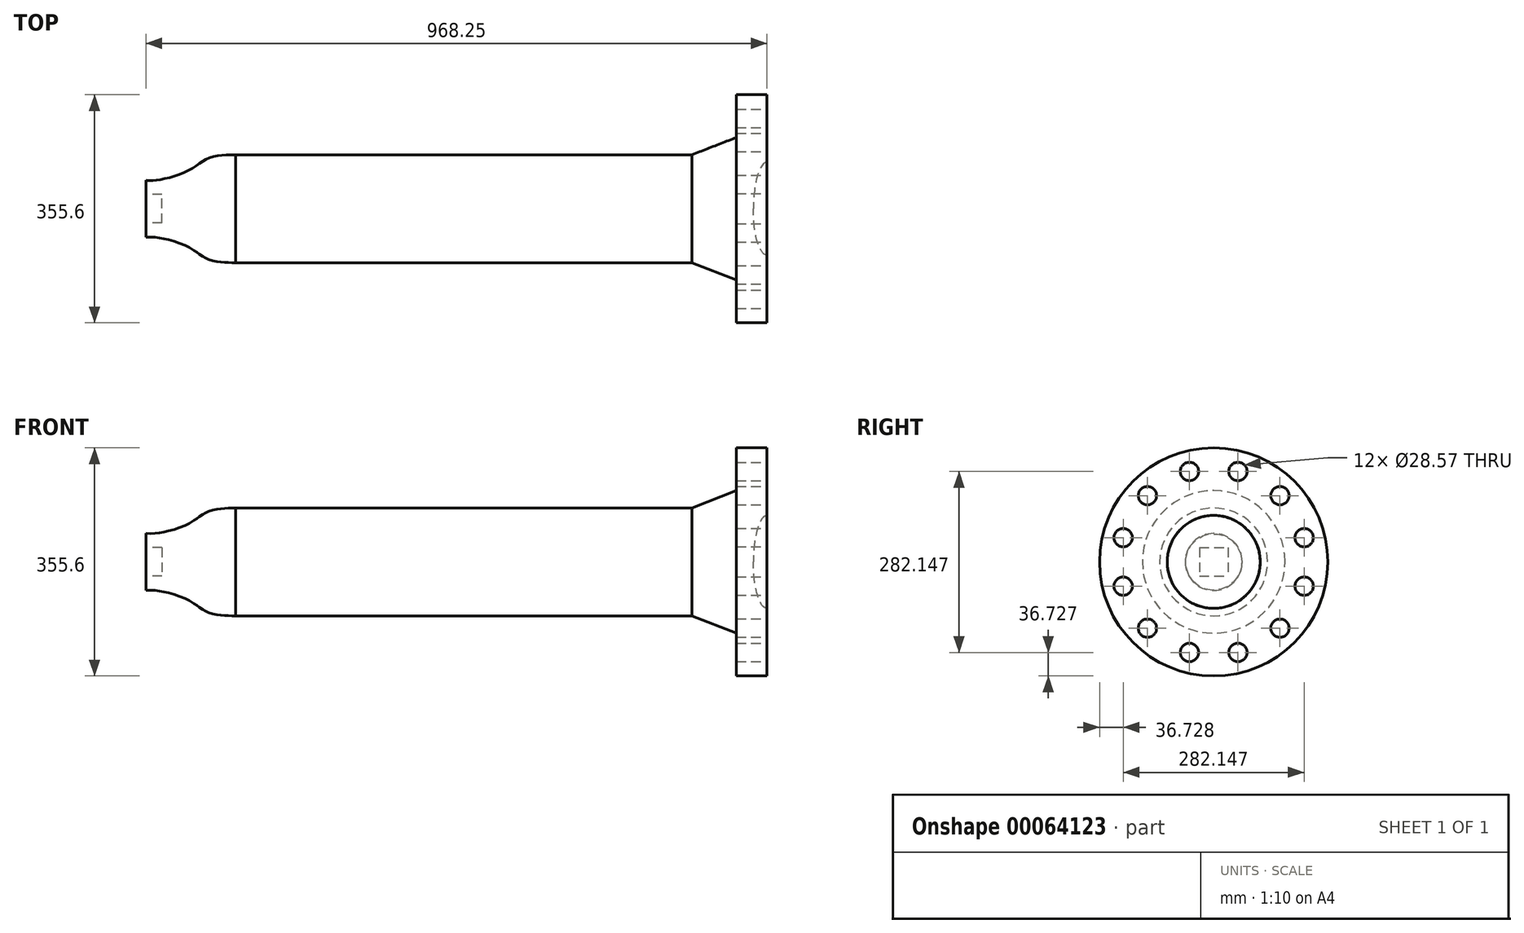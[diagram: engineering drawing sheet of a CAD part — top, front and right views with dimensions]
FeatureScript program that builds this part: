
annotation { "Feature Type Name" : "Feature", "Feature Type Description" : "" }
export const myFeature = defineFeature(function(context is Context, id is Id, definition is map)
    precondition{}
    {
        {
            var Q0;
            Q0=qCreatedBy(makeId("Top.planeOp"),FACE);
            var sketch = newSketch(context, id + "F0", { "sketchPlane" : qUnion([Q0])});
            skLineSegment(sketch, "E0.bottom", {"start": v(355.6, 55.78) * mm, "end": v(-355.6, 55.78) * mm});
            skLineSegment(sketch, "E0.left", {"start": v(355.6, 55.78) * mm, "end": v(355.6, -28.36) * mm});
            skLineSegment(sketch, "E0.right", {"start": v(-355.6, 55.78) * mm, "end": v(-355.6, -28.36) * mm});
            skPoint(sketch, "E0.middle", {"position": v(0, -28.36) * mm});
            skLineSegment(sketch, "E1", {"start": v(-355.6, -28.36) * mm, "end": v(-495.3, -28.36) * mm});
            skLineSegment(sketch, "E2", {"start": v(-495.3, -28.36) * mm, "end": v(-495.3, 16.1) * mm});
            skFitSpline(sketch, "E3", {"points": [v(-495.3, 16.1) * mm, v(-480.3, 16.1) * mm, v(-430.85, 30.2) * mm, v(-397.55, 50.39) * mm, v(-355.6, 55.78) * mm], "startDerivative": vector(75.86, -6.63) * mm, "endDerivative": vector(164.84, 3.12) * mm});
            skLineSegment(sketch, "E4", {"start": v(-355.6, -28.36) * mm, "end": v(355.6, -28.36) * mm});
            skLineSegment(sketch, "E5", {"start": v(0, 55.78) * mm, "end": v(0, -112.5) * mm, "construction": true});
            skLineSegment(sketch, "E6", {"start": v(355.6, -28.36) * mm, "end": v(472.95, -28.36) * mm});
            skLineSegment(sketch, "E7", {"start": v(472.95, -28.36) * mm, "end": v(472.95, 149.44) * mm});
            skLineSegment(sketch, "E8", {"start": v(472.95, 149.44) * mm, "end": v(425.2, 149.44) * mm});
            skLineSegment(sketch, "E9", {"start": v(425.2, 149.44) * mm, "end": v(425.2, 82.77) * mm});
            skLineSegment(sketch, "E10", {"start": v(425.2, 82.77) * mm, "end": v(355.6, 55.78) * mm});
            skEllipticalArc(sketch, "E11", {});
            const initialGuessF0  = {"E11": [0.472948, -0.028358574647295482, 0, 1, 0.07247824563442469, 0.021333515674718143, 0, 1.5707963267948966]};
            skSetInitialGuess(sketch, initialGuessF0);
            skSolve(sketch);
        }
        {
            var Q0;
            Q0=makeQuery(id+"F0.imprint","IMPRINT",FACE,{"disambiguationData":[TD([[makeQuery(id+"F0.imprint","IMPRINT",EDGE,{"derivedFrom":sQuery(id+"F0.wireOp",EDGE,"E0.right")}),-1.0]])]});
            var Q1;
            Q1=makeQuery(id+"F0.imprint","IMPRINT",FACE,{"disambiguationData":[TD([[makeQuery(id+"F0.imprint","IMPRINT",EDGE,{"derivedFrom":sQuery(id+"F0.wireOp",EDGE,"E0.bottom")}),1.0]])]});
            var Q2;
            Q2=makeQuery(id+"F0.imprint","IMPRINT",FACE,{"disambiguationData":[TD([[makeQuery(id+"F0.imprint","IMPRINT",EDGE,{"derivedFrom":sQuery(id+"F0.wireOp",EDGE,"E0.left")}),1.0]])]});
            var Q3;
            Q3=sQuery(id+"F0.wireOp",EDGE,"E1");
            revolve(context, id + "F1", {"entities" : qUnion([Q0, Q1, Q2]), "axis" : qUnion([Q3]), "revolveType" : RevolveType.FULL});
        }
        {
            var Q0;
            Q0=makeQuery(id+"F1.opRevolve","SWEPT_FACE",FACE,{"disambiguationData":[OSD([sQuery(id+"F0.wireOp",EDGE,"E2")])]});
            var sketch = newSketch(context, id + "F2", { "sketchPlane" : qUnion([Q0])});
            skLineSegment(sketch, "E12.bottom", {"start": v(50.58, 22.23) * mm, "end": v(6.13, 22.22) * mm});
            skLineSegment(sketch, "E12.top", {"start": v(50.58, -22.23) * mm, "end": v(6.13, -22.23) * mm});
            skLineSegment(sketch, "E12.left", {"start": v(50.58, 22.23) * mm, "end": v(50.58, -22.23) * mm});
            skLineSegment(sketch, "E12.right", {"start": v(6.13, 22.23) * mm, "end": v(6.13, -22.23) * mm});
            skPoint(sketch, "E12.middle", {"position": v(28.36, 0) * mm});
            skSolve(sketch);
        }
        {
            var Q0;
            Q0=makeQuery(id+"F2.imprint","IMPRINT",FACE,{"disambiguationData":[TD([[makeQuery(id+"F2.imprint","IMPRINT",EDGE,{"derivedFrom":sQuery(id+"F2.wireOp",EDGE,"E12.bottom")}),1.0]])]});
            extrude(context, id + "F3", {"entities" : qUnion([Q0]), "operationType" : NewBodyOperationType.REMOVE, "oppositeDirection" : true, "depth" : 25.4 * mm, "offsetDistance" : 25.4 * mm});
        }
        {
            var Q0;
            Q0=makeQuery(id+"F1.opRevolve","SWEPT_FACE",FACE,{"disambiguationData":[OSD([sQuery(id+"F0.wireOp",EDGE,"E7")])]});
            var sketch = newSketch(context, id + "F4", { "sketchPlane" : qUnion([Q0])});
            skCircle(sketch, "E13", {"center": v(-28.36, 0) * mm, "radius": 146.05 * mm, "construction": true});
            skLineSegment(sketch, "E14", {"start": v(-28.36, 0) * mm, "end": v(185.04, 0) * mm, "construction": true});
            skLineSegment(sketch, "E15", {"start": v(-28.36, 0) * mm, "end": v(183.38, 56.74) * mm, "construction": true});
            skCircle(sketch, "E16", {"center": v(112.71, 37.8) * mm, "radius": 14.29 * mm});
            skCircle(sketch, "E17.1.0", {"center": v(74.91, 103.27) * mm, "radius": 14.29 * mm});
            skCircle(sketch, "E17.2.0", {"center": v(9.44, 141.07) * mm, "radius": 14.29 * mm});
            skCircle(sketch, "E17.3.0", {"center": v(-66.16, 141.07) * mm, "radius": 14.29 * mm});
            skCircle(sketch, "E17.4.0", {"center": v(-131.63, 103.27) * mm, "radius": 14.29 * mm});
            skCircle(sketch, "E17.5.0", {"center": v(-169.43, 37.8) * mm, "radius": 14.29 * mm});
            skCircle(sketch, "E17.6.0", {"center": v(-169.43, -37.8) * mm, "radius": 14.29 * mm});
            skCircle(sketch, "E17.7.0", {"center": v(-131.63, -103.27) * mm, "radius": 14.29 * mm});
            skCircle(sketch, "E17.8.0", {"center": v(-66.16, -141.07) * mm, "radius": 14.29 * mm});
            skCircle(sketch, "E17.9.0", {"center": v(9.44, -141.07) * mm, "radius": 14.29 * mm});
            skCircle(sketch, "E17.10.0", {"center": v(74.91, -103.27) * mm, "radius": 14.29 * mm});
            skCircle(sketch, "E17.11.0", {"center": v(112.71, -37.8) * mm, "radius": 14.29 * mm});
            skSolve(sketch);
        }
        {
            var Q0;
            Q0=makeQuery(id+"F4.imprint","IMPRINT",FACE,{"disambiguationData":[TD([[makeQuery(id+"F4.imprint","IMPRINT",EDGE,{"derivedFrom":sQuery(id+"F4.wireOp",EDGE,"E17.4.0")}),1.0]])]});
            var Q1;
            Q1=makeQuery(id+"F4.imprint","IMPRINT",FACE,{"disambiguationData":[TD([[makeQuery(id+"F4.imprint","IMPRINT",EDGE,{"derivedFrom":sQuery(id+"F4.wireOp",EDGE,"E17.3.0")}),1.0]])]});
            var Q2;
            Q2=makeQuery(id+"F4.imprint","IMPRINT",FACE,{"disambiguationData":[TD([[makeQuery(id+"F4.imprint","IMPRINT",EDGE,{"derivedFrom":sQuery(id+"F4.wireOp",EDGE,"E17.2.0")}),1.0]])]});
            var Q3;
            Q3=makeQuery(id+"F4.imprint","IMPRINT",FACE,{"disambiguationData":[TD([[makeQuery(id+"F4.imprint","IMPRINT",EDGE,{"derivedFrom":sQuery(id+"F4.wireOp",EDGE,"E17.1.0")}),1.0]])]});
            var Q4;
            Q4=makeQuery(id+"F4.imprint","IMPRINT",FACE,{"disambiguationData":[TD([[makeQuery(id+"F4.imprint","IMPRINT",EDGE,{"derivedFrom":sQuery(id+"F4.wireOp",EDGE,"E16")}),1.0]])]});
            var Q5;
            Q5=makeQuery(id+"F4.imprint","IMPRINT",FACE,{"disambiguationData":[TD([[makeQuery(id+"F4.imprint","IMPRINT",EDGE,{"derivedFrom":sQuery(id+"F4.wireOp",EDGE,"E17.11.0")}),1.0]])]});
            var Q6;
            Q6=makeQuery(id+"F4.imprint","IMPRINT",FACE,{"disambiguationData":[TD([[makeQuery(id+"F4.imprint","IMPRINT",EDGE,{"derivedFrom":sQuery(id+"F4.wireOp",EDGE,"E17.10.0")}),1.0]])]});
            var Q7;
            Q7=makeQuery(id+"F4.imprint","IMPRINT",FACE,{"disambiguationData":[TD([[makeQuery(id+"F4.imprint","IMPRINT",EDGE,{"derivedFrom":sQuery(id+"F4.wireOp",EDGE,"E17.9.0")}),1.0]])]});
            var Q8;
            Q8=makeQuery(id+"F4.imprint","IMPRINT",FACE,{"disambiguationData":[TD([[makeQuery(id+"F4.imprint","IMPRINT",EDGE,{"derivedFrom":sQuery(id+"F4.wireOp",EDGE,"E17.8.0")}),1.0]])]});
            var Q9;
            Q9=makeQuery(id+"F4.imprint","IMPRINT",FACE,{"disambiguationData":[TD([[makeQuery(id+"F4.imprint","IMPRINT",EDGE,{"derivedFrom":sQuery(id+"F4.wireOp",EDGE,"E17.7.0")}),1.0]])]});
            var Q10;
            Q10=makeQuery(id+"F4.imprint","IMPRINT",FACE,{"disambiguationData":[TD([[makeQuery(id+"F4.imprint","IMPRINT",EDGE,{"derivedFrom":sQuery(id+"F4.wireOp",EDGE,"E17.6.0")}),1.0]])]});
            var Q11;
            Q11=makeQuery(id+"F4.imprint","IMPRINT",FACE,{"disambiguationData":[TD([[makeQuery(id+"F4.imprint","IMPRINT",EDGE,{"derivedFrom":sQuery(id+"F4.wireOp",EDGE,"E17.5.0")}),1.0]])]});
            var Q12;
            Q12=sQuery(id+"F4.wireOp",EDGE,"E13");
            var Q13;
            Q13=sQuery(id+"F4.wireOp",EDGE,"E17.4.0");
            var Q14;
            Q14=sQuery(id+"F4.wireOp",EDGE,"E17.3.0");
            var Q15;
            Q15=sQuery(id+"F4.wireOp",EDGE,"E17.2.0");
            var Q16;
            Q16=sQuery(id+"F4.wireOp",EDGE,"E17.1.0");
            var Q17;
            Q17=sQuery(id+"F4.wireOp",EDGE,"E16");
            var Q18;
            Q18=sQuery(id+"F4.wireOp",EDGE,"E17.11.0");
            var Q19;
            Q19=sQuery(id+"F4.wireOp",EDGE,"E17.10.0");
            var Q20;
            Q20=sQuery(id+"F4.wireOp",EDGE,"E17.9.0");
            var Q21;
            Q21=sQuery(id+"F4.wireOp",EDGE,"E17.8.0");
            var Q22;
            Q22=sQuery(id+"F4.wireOp",EDGE,"E17.7.0");
            var Q23;
            Q23=sQuery(id+"F4.wireOp",EDGE,"E17.6.0");
            var Q24;
            Q24=sQuery(id+"F4.wireOp",EDGE,"E17.5.0");
            extrude(context, id + "F5", {"entities" : qUnion([Q0, Q1, Q2, Q3, Q4, Q5, Q6, Q7, Q8, Q9, Q10, Q11]), "operationType" : NewBodyOperationType.REMOVE, "surfaceEntities" : qUnion([Q12, Q13, Q14, Q15, Q16, Q17, Q18, Q19, Q20, Q21, Q22, Q23, Q24]), "endBound" : BoundingType.THROUGH_ALL, "oppositeDirection" : true, "depth" : 25.4 * mm, "offsetDistance" : 25.4 * mm});
        }
    });
